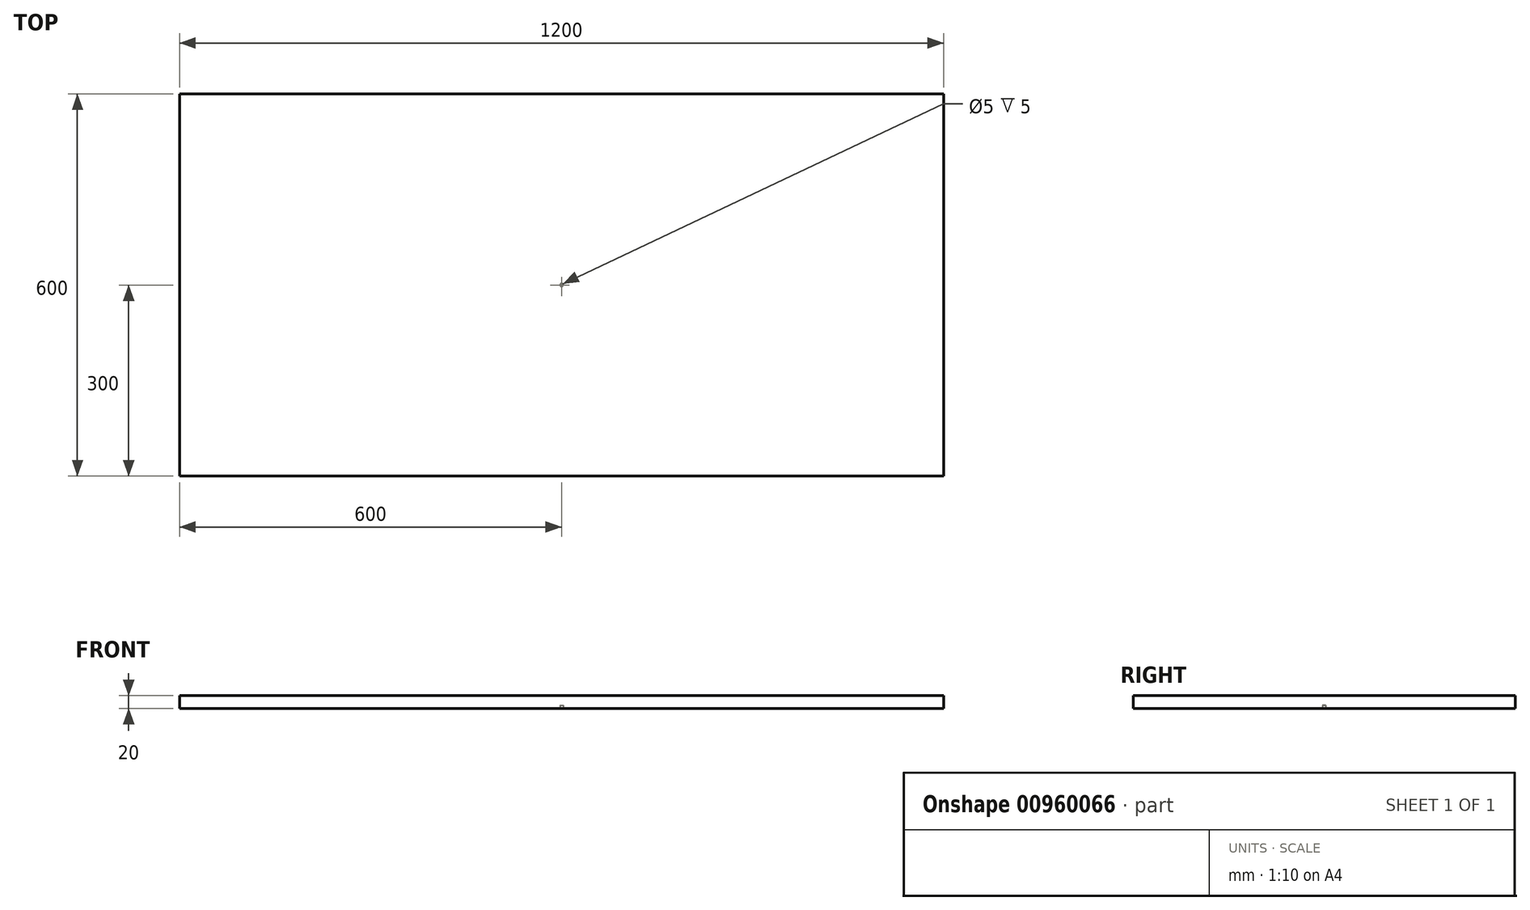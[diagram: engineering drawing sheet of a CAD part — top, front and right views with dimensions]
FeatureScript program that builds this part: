
annotation { "Feature Type Name" : "Feature", "Feature Type Description" : "" }
export const myFeature = defineFeature(function(context is Context, id is Id, definition is map)
    precondition{}
    {
        {
            var Q0;
            Q0=qCreatedBy(makeId("Top.planeOp"),FACE);
            var sketch = newSketch(context, id + "F0", { "sketchPlane" : qUnion([Q0])});
            skLineSegment(sketch, "E0.bottom", {"start": v(600, -300) * mm, "end": v(-600, -300) * mm});
            skLineSegment(sketch, "E0.top", {"start": v(600, 300) * mm, "end": v(-600, 300) * mm});
            skLineSegment(sketch, "E0.left", {"start": v(600, -300) * mm, "end": v(600, 300) * mm});
            skLineSegment(sketch, "E0.right", {"start": v(-600, -300) * mm, "end": v(-600, 300) * mm});
            skPoint(sketch, "E0.middle", {"position": v(0, 0) * mm});
            skSolve(sketch);
        }
        {
            var Q0;
            Q0 = qSketchRegion(id + "F0", true);
            extrude(context, id + "F1", {"entities" : qUnion([Q0]), "depth" : 20 * mm, "offsetDistance" : 25 * mm});
        }
        {
            var Q0;
            Q0=makeQuery(id+"F1.opExtrude","CAP_FACE",FACE,{"disambiguationData":[OSD([sQuery(id+"F0.wireOp",EDGE,"E0.bottom"),sQuery(id+"F0.wireOp",EDGE,"E0.top"),sQuery(id+"F0.wireOp",EDGE,"E0.left"),sQuery(id+"F0.wireOp",EDGE,"E0.right")])],"isStart":true});
            var sketch = newSketch(context, id + "F2", { "sketchPlane" : qUnion([Q0])});
            skCircle(sketch, "E1", {"center": v(0, 0) * mm, "radius": 2.5 * mm});
            skSolve(sketch);
        }
        {
            var Q0;
            Q0=makeQuery(id+"F2.imprint","IMPRINT",FACE,{"disambiguationData":[TD([[makeQuery(id+"F2.imprint","IMPRINT",EDGE,{"derivedFrom":sQuery(id+"F2.wireOp",EDGE,"E1")}),1.0]])]});
            extrude(context, id + "F3", {"entities" : qUnion([Q0]), "operationType" : NewBodyOperationType.REMOVE, "oppositeDirection" : true, "depth" : 5 * mm, "offsetDistance" : 25 * mm});
        }
    });
